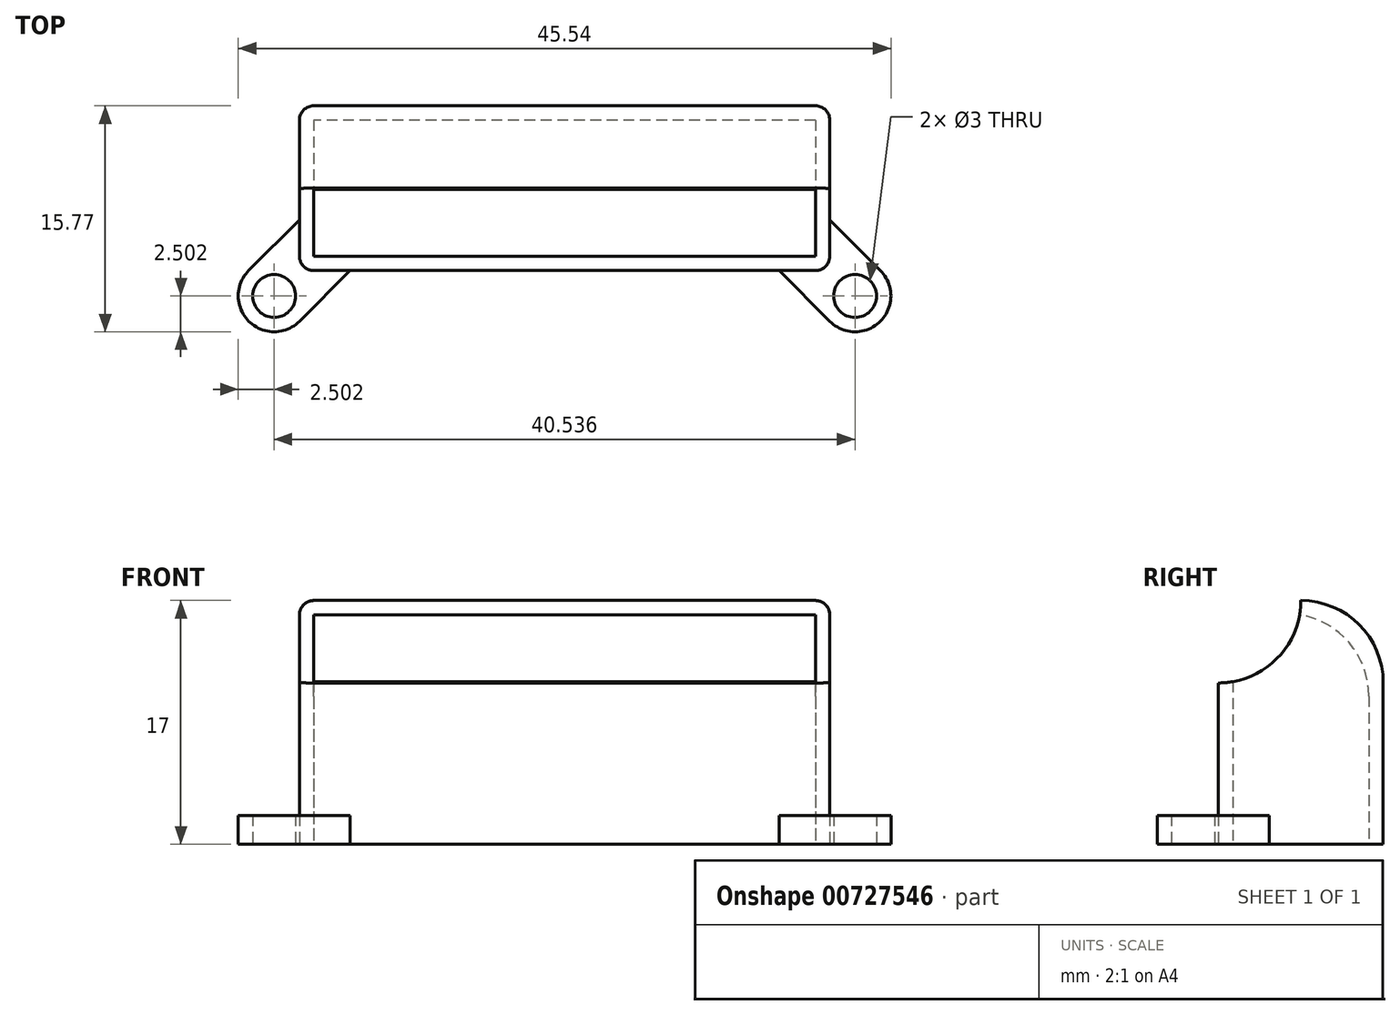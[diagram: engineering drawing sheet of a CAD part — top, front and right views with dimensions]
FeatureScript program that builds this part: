
annotation { "Feature Type Name" : "Feature", "Feature Type Description" : "" }
export const myFeature = defineFeature(function(context is Context, id is Id, definition is map)
    precondition{}
    {
        {
            var Q0;
            Q0=qCreatedBy(makeId("Top.planeOp"),FACE);
            var sketch = newSketch(context, id + "F0", { "sketchPlane" : qUnion([Q0])});
            skCircle(sketch, "E0", {"center": v(-20.27, -7.52) * mm, "radius": 1.5 * mm});
            skCircle(sketch, "E1", {"center": v(20.27, -7.52) * mm, "radius": 1.5 * mm});
            skLineSegment(sketch, "E2", {"start": v(-22.04, -5.75) * mm, "end": v(-18.5, -2.21) * mm});
            skLineSegment(sketch, "E3", {"start": v(-18.5, -9.29) * mm, "end": v(-14.96, -5.75) * mm});
            skLineSegment(sketch, "E4", {"start": v(18.5, -2.21) * mm, "end": v(22.04, -5.75) * mm});
            skLineSegment(sketch, "E5", {"start": v(14.96, -5.75) * mm, "end": v(18.5, -9.29) * mm});
            skLineSegment(sketch, "E6", {"start": v(-18.5, -5.75) * mm, "end": v(-20.27, -7.52) * mm});
            skLineSegment(sketch, "E7", {"start": v(18.5, -5.75) * mm, "end": v(20.27, -7.52) * mm});
            skLineSegment(sketch, "E8.bottom", {"start": v(18.5, 5.75) * mm, "end": v(-18.5, 5.75) * mm});
            skLineSegment(sketch, "E8.top", {"start": v(18.5, -5.75) * mm, "end": v(-18.5, -5.75) * mm});
            skLineSegment(sketch, "E8.left", {"start": v(18.5, 5.75) * mm, "end": v(18.5, -5.75) * mm});
            skLineSegment(sketch, "E8.right", {"start": v(-18.5, 5.75) * mm, "end": v(-18.5, -5.75) * mm});
            skPoint(sketch, "E8.middle", {"position": v(0, 0) * mm});
            skCircle(sketch, "E9", {"center": v(-20.27, -7.52) * mm, "radius": 2.5 * mm});
            skCircle(sketch, "E10", {"center": v(20.27, -7.52) * mm, "radius": 2.5 * mm});
            skSolve(sketch);
        }
        {
            var Q0;
            {var subQ3=sQuery(id+"F0.wireOp",EDGE,"E8.bottom");Q0=makeQuery(id+"F0.imprint","IMPRINT",FACE,{"disambiguationData":[TD([[makeQuery(id+"F0.imprint","IMPRINT",EDGE,{"derivedFrom":subQ3}),1.0]])]});}
            extrude(context, id + "F1", {"entities" : qUnion([Q0]), "depth" : 17 * mm, "offsetDistance" : 25 * mm});
        }
        {
            var Q0;
            Q0=makeQuery(id+"F1.opExtrude","SWEPT_FACE",FACE,{"disambiguationData":[OSD([sQuery(id+"F0.wireOp",EDGE,"E8.left")])]});
            var sketch = newSketch(context, id + "F2", { "sketchPlane" : qUnion([Q0])});
            skCircle(sketch, "E11", {"center": v(-5.75, 17) * mm, "radius": 5.75 * mm});
            skSolve(sketch);
        }
        {
            var Q0;
            Q0=makeQuery(id+"F1.opExtrude","CAP_FACE",FACE,{"disambiguationData":[OSD([sQuery(id+"F0.wireOp",EDGE,"E8.bottom"),sQuery(id+"F0.wireOp",EDGE,"E8.top"),sQuery(id+"F0.wireOp",EDGE,"E8.left"),sQuery(id+"F0.wireOp",EDGE,"E8.right")])],"isStart":true});
            shell(context, id + "F3", {"entities" : qUnion([Q0]), "thickness" : 1 * mm});
        }
        {
            var Q0;
            {var subQ0=sQuery(id+"F2.wireOp",EDGE,"E11");var subQ1=sQuery(id+"F0.wireOp",EDGE,"E8.left");var subQ4=makeQuery(id+"F1.opExtrude","CAP_EDGE",EDGE,{"disambiguationData":[OSD([subQ1])],"isStart":false});var subQ5=makeQuery(id+"F2.imprint","INTERSECT",VERTEX,{"derivedFrom":[subQ4,subQ0]});Q0=makeQuery(id+"F2.imprint","IMPRINT",FACE,{"disambiguationData":[TD([[makeQuery(id+"F2.imprint","IMPRINT",EDGE,{"disambiguationData":[TD([[subQ5,1.0]])],"derivedFrom":subQ0}),1.0]])]});}
            extrude(context, id + "F4", {"entities" : qUnion([Q0]), "operationType" : NewBodyOperationType.REMOVE, "endBound" : BoundingType.THROUGH_ALL, "oppositeDirection" : true, "depth" : 25 * mm, "offsetDistance" : 25 * mm});
        }
        {
            var Q0;
            Q0=makeQuery(id+"F1.opExtrude","CAP_EDGE",EDGE,{"disambiguationData":[OSD([sQuery(id+"F0.wireOp",EDGE,"E8.bottom")])],"isStart":false});
            var Q1;
            {var subQ0=sQuery(id+"F0.wireOp",EDGE,"E8.bottom");Q1=makeQuery(id+"F3.opShell","OFFSET_EDGE",EDGE,{"disambiguationData":[OSD([subQ0]),TDD([makeQuery(id+"F1.opExtrude","CAP_EDGE",EDGE,{"disambiguationData":[OSD([subQ0])],"isStart":false})])]});}
            fillet(context, id + "F5", {"entities" : qUnion([Q0, Q1]), "radius" : 5.75 * mm, "allowEdgeOverflow" : false});
        }
        {
            var Q0;
            {var subQ0=sQuery(id+"F0.wireOp",EDGE,"E2");Q0=makeQuery(id+"F0.imprint","IMPRINT",FACE,{"disambiguationData":[TD([[makeQuery(id+"F0.imprint","IMPRINT",EDGE,{"derivedFrom":subQ0}),-1.0]])]});}
            var Q1;
            {var subQ0=sQuery(id+"F0.wireOp",EDGE,"E3");Q1=makeQuery(id+"F0.imprint","IMPRINT",FACE,{"disambiguationData":[TD([[makeQuery(id+"F0.imprint","IMPRINT",EDGE,{"derivedFrom":subQ0}),1.0]])]});}
            var Q2;
            Q2=makeQuery(id+"F0.imprint","IMPRINT",FACE,{"disambiguationData":[TD([[makeQuery(id+"F0.imprint","IMPRINT",EDGE,{"derivedFrom":sQuery(id+"F0.wireOp",EDGE,"E0")}),-1.0]])]});
            var Q3;
            {var subQ0=sQuery(id+"F0.wireOp",EDGE,"E5");Q3=makeQuery(id+"F0.imprint","IMPRINT",FACE,{"disambiguationData":[TD([[makeQuery(id+"F0.imprint","IMPRINT",EDGE,{"derivedFrom":subQ0}),1.0]])]});}
            var Q4;
            {var subQ0=sQuery(id+"F0.wireOp",EDGE,"E4");Q4=makeQuery(id+"F0.imprint","IMPRINT",FACE,{"disambiguationData":[TD([[makeQuery(id+"F0.imprint","IMPRINT",EDGE,{"derivedFrom":subQ0}),-1.0]])]});}
            var Q5;
            Q5=makeQuery(id+"F0.imprint","IMPRINT",FACE,{"disambiguationData":[TD([[makeQuery(id+"F0.imprint","IMPRINT",EDGE,{"derivedFrom":sQuery(id+"F0.wireOp",EDGE,"E1")}),-1.0]])]});
            extrude(context, id + "F6", {"entities" : qUnion([Q0, Q1, Q2, Q3, Q4, Q5]), "operationType" : NewBodyOperationType.ADD, "depth" : 2 * mm, "offsetDistance" : 25 * mm});
        }
        {
            var Q0;
            Q0=makeQuery(id+"F1.opExtrude","SWEPT_EDGE",EDGE,{"disambiguationData":[OSD([sQuery(id+"F0.wireOp",EDGE,"E8.top"),sQuery(id+"F0.wireOp",EDGE,"E8.right"),sQuery(id+"F0.wireOp",EDGE,"E9")])]});
            var Q1;
            Q1=makeQuery(id+"F1.opExtrude","SWEPT_EDGE",EDGE,{"disambiguationData":[OSD([sQuery(id+"F0.wireOp",EDGE,"E8.top"),sQuery(id+"F0.wireOp",EDGE,"E8.left"),sQuery(id+"F0.wireOp",EDGE,"E10")])]});
            var Q2;
            Q2=makeQuery(id+"F1.opExtrude","SWEPT_EDGE",EDGE,{"disambiguationData":[OSD([sQuery(id+"F0.wireOp",EDGE,"E8.bottom"),sQuery(id+"F0.wireOp",EDGE,"E8.left")])]});
            var Q3;
            Q3=makeQuery(id+"F1.opExtrude","SWEPT_EDGE",EDGE,{"disambiguationData":[OSD([sQuery(id+"F0.wireOp",EDGE,"E8.bottom"),sQuery(id+"F0.wireOp",EDGE,"E8.right")])]});
            fillet(context, id + "F7", {"entities" : qUnion([Q0, Q1, Q2, Q3]), "radius" : 1 * mm, "tangentPropagation" : true, "allowEdgeOverflow" : false});
        }
    });
